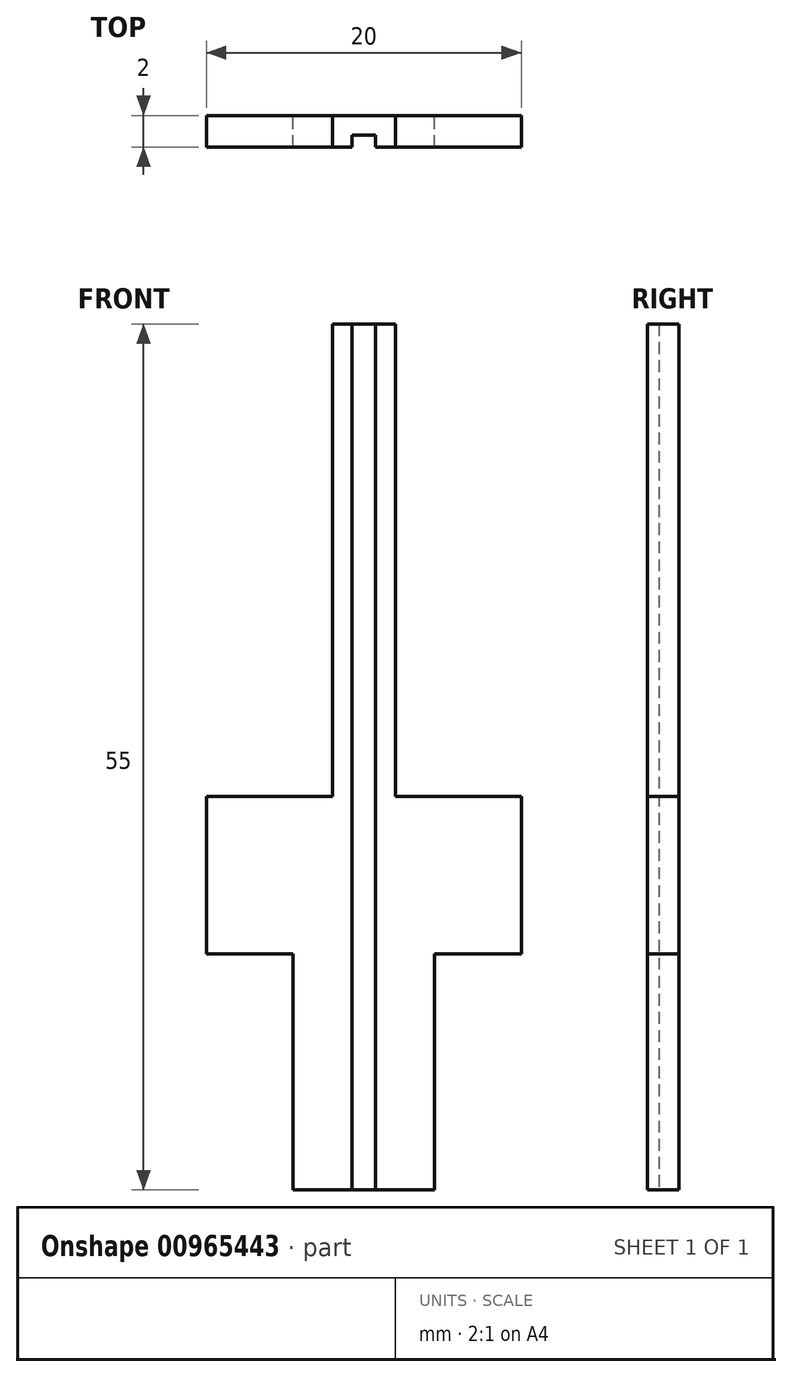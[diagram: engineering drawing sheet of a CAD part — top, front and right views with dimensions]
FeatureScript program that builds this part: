
annotation { "Feature Type Name" : "Feature", "Feature Type Description" : "" }
export const myFeature = defineFeature(function(context is Context, id is Id, definition is map)
    precondition{}
    {
        {
            var Q0;
            Q0=qCreatedBy(makeId("Front.planeOp"),FACE);
            var sketch = newSketch(context, id + "F0", { "sketchPlane" : qUnion([Q0])});
            skLineSegment(sketch, "E0.bottom", {"start": v(10, 5) * mm, "end": v(2, 5) * mm});
            skLineSegment(sketch, "E0.top", {"start": v(10, -5) * mm, "end": v(4.5, -5) * mm});
            skLineSegment(sketch, "E0.left", {"start": v(10, 5) * mm, "end": v(10, -5) * mm});
            skLineSegment(sketch, "E0.right", {"start": v(-10, 5) * mm, "end": v(-10, -5) * mm});
            skPoint(sketch, "E0.middle", {"position": v(0, 0) * mm});
            skLineSegment(sketch, "E1.bottom", {"start": v(2, 35) * mm, "end": v(-2, 35) * mm});
            skLineSegment(sketch, "E1.left", {"start": v(2, 35) * mm, "end": v(2, 5) * mm});
            skLineSegment(sketch, "E1.right", {"start": v(-2, 35) * mm, "end": v(-2, 5) * mm});
            skPoint(sketch, "E1.middle", {"position": v(0, 5) * mm});
            skLineSegment(sketch, "E2.top", {"start": v(4.5, -20) * mm, "end": v(-4.5, -20) * mm});
            skLineSegment(sketch, "E2.left", {"start": v(4.5, -5) * mm, "end": v(4.5, -20) * mm});
            skLineSegment(sketch, "E2.right", {"start": v(-4.5, -5) * mm, "end": v(-4.5, -20) * mm});
            skPoint(sketch, "E2.middle", {"position": v(0, -12.5) * mm});
            skPoint(sketch, "E2.middle.positionSnap0", {"position": v(0, -5) * mm});
            skPoint(sketch, "E2.centerSnap0", {"position": v(0, -5) * mm});
            skPoint(sketch, "E3.orphan", {"position": v(2, -25) * mm});
            skPoint(sketch, "E4.orphan", {"position": v(-2, -25) * mm});
            skLineSegment(sketch, "E5.trimOffspring", {"start": v(-4.5, -5) * mm, "end": v(-10, -5) * mm});
            skLineSegment(sketch, "E6.trimOffspring", {"start": v(-2, 5) * mm, "end": v(-10, 5) * mm});
            skSolve(sketch);
        }
        {
            var Q0;
            Q0 = qSketchRegion(id + "F0", true);
            extrude(context, id + "F1", {"entities" : qUnion([Q0]), "depth" : 2 * mm, "offsetDistance" : 25 * mm});
        }
        {
            var Q0;
            Q0=makeQuery(id+"F1.opExtrude","CAP_FACE",FACE,{"disambiguationData":[OSD([sQuery(id+"F0.wireOp",EDGE,"E0.bottom"),sQuery(id+"F0.wireOp",EDGE,"E0.top"),sQuery(id+"F0.wireOp",EDGE,"E0.left"),sQuery(id+"F0.wireOp",EDGE,"E0.right"),sQuery(id+"F0.wireOp",EDGE,"E1.bottom"),sQuery(id+"F0.wireOp",EDGE,"E1.left"),sQuery(id+"F0.wireOp",EDGE,"E1.right"),sQuery(id+"F0.wireOp",EDGE,"E2.top"),sQuery(id+"F0.wireOp",EDGE,"E2.left"),sQuery(id+"F0.wireOp",EDGE,"E2.right"),sQuery(id+"F0.wireOp",EDGE,"E5.trimOffspring"),sQuery(id+"F0.wireOp",EDGE,"E6.trimOffspring")])],"isStart":false});
            var sketch = newSketch(context, id + "F2", { "sketchPlane" : qUnion([Q0])});
            skLineSegment(sketch, "E7.bottom", {"start": v(0.75, 40.5) * mm, "end": v(-0.75, 40.5) * mm});
            skLineSegment(sketch, "E7.top", {"start": v(0.75, -40.5) * mm, "end": v(-0.75, -40.5) * mm});
            skLineSegment(sketch, "E7.left", {"start": v(0.75, 40.5) * mm, "end": v(0.75, -40.5) * mm});
            skLineSegment(sketch, "E7.right", {"start": v(-0.75, 40.5) * mm, "end": v(-0.75, -40.5) * mm});
            skPoint(sketch, "E7.middle", {"position": v(0, 0) * mm});
            skSolve(sketch);
        }
        {
            var Q0;
            Q0 = qSketchRegion(id + "F2", true);
            extrude(context, id + "F3", {"entities" : qUnion([Q0]), "operationType" : NewBodyOperationType.REMOVE, "oppositeDirection" : true, "depth" : 0.75 * mm, "offsetDistance" : 25 * mm});
        }
    });
